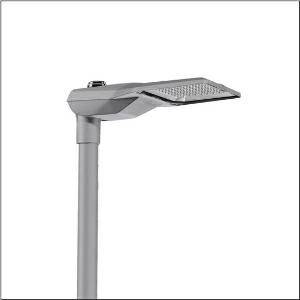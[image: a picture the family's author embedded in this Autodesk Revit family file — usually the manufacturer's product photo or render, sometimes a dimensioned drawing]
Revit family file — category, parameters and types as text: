
# Revit family: streetlight_sl_21_midi___st0_5a_5xe7b47n08lb_dab4
name_source: partatom
category: Lighting Fixtures
units: mm (PartAtom-declared; Revit-internal decimal feet)

## family parameters
Cut with Voids When Loaded = No
Host = Face
Light Source = No
Part Type = Normal
Room Calculation Point = No
Round Connector Dimension = Use Diameter
Shared = No

## types (1)
- --- (1 x LED, 14950 lm, 98.3 W, 4000K)
    Apparent Load = 98 VA
    CIE Flux Codes = 41 75 97 100 100
    Color Rendering = 70
    Color Temperature = 4000K
    Default Elevation = 1800 mm
    Description = Streetlight SL 21 midi, mast luminaire, primary light control with lens, of PMMA, primary optical cover: cover, of toughened safety glass, transparent, light distribution: ST0.5a, light emission: direct distribution, primary light characteristic: asymmetric, installation type: side-entry, LED, 3G 2.5mm², High Power LED, rated luminous flux: 14.950lm, luminous efficacy: 152lm/W, light colour: 740, colour temperature: 4000K, control: overheat protection, pre-setting: linear dimming characteristic, constant luminous flux control, time-dependent luminous flux control, flexible luminous flux parameterisation, mains connection: 220..240V, AC, 50/60Hz, connection cable pre-assembled, cable length: 10,5m, wiring characteristics: H05VV-F, start of lifetime: 98W, end of service life: 101W, reduction: 45W, luminaire housing, of diecast aluminium (EN AC-44300), powder-coated, Siteco® metallic grey (DB 702S), corrosivity category C5 mid according to DIN EN ISO 12944, multi-level sealing system, sealing non-destructively replaceable, inclination adjustable: 0°, 5°, 10°, 15°, length: 644mm, width: 335mm, height: 110mm, spigot size: 42mm (side-entry), protection rating (complete): IP66, insulation class (complete): insulation class I (protective earthing), certification: CE, ENEC, ENEC+, VDE, impact resistance: IK09, permissible operating ambient temperature for outdoor applications: -40..+50°C, standard-compliant lighting for roads and squares, packaging unit: 1 piece

Light Distribution: ST0.5a
    Height = 111 mm
    Lamp = 1 x LED
    Lamp Light Flux = 14950 lm
    Lamp Power = 98.3 W
    Lamp count = 1
    Length = 644 mm
    Luminous efficacy = 152 lm/W
    Manufacturer = Siteco
    ModVariant = No
    Model = 5XE7B47N08LB
    Number of Poles = 1
    OnlyDefault = Yes
    Power Factor = 1
    Product Name = Streetlight SL 21 midi | ST0.5a
    Product group = mast luminaire | pylon top
    ProductGroupID = 6100
    Protection Class = Protection class I
    Protection Degree = IP 66
    RLX_Detail_Level = 1
    RLX_Emergency_Light_Flux = 0 lm
    RLX_Emergency_Type = 0
    RLX_Emergency_Type_DB = No
    RlxData = <blob elided: 101369 chars, md5=26aed3c0>
    Socket = socket
    Standby Power = 0 W
    System Light Flux = 14950 lm
    System Power = 98 W
    Type Comments = factory setting: luminous flux: 100 % | dim-lin: 254 | 1020 mA
    Type Image = l_1294377.jpg
    URL = http://relux.com
    VarID = @adj_107103
    Voltage = 0 V
    Weight = 0.00 kg
    Width = 336 mm

## geometry (parser evidence)
native form markers: Blend x4, Sweep x10
no freeform markers — native parametric forms only
